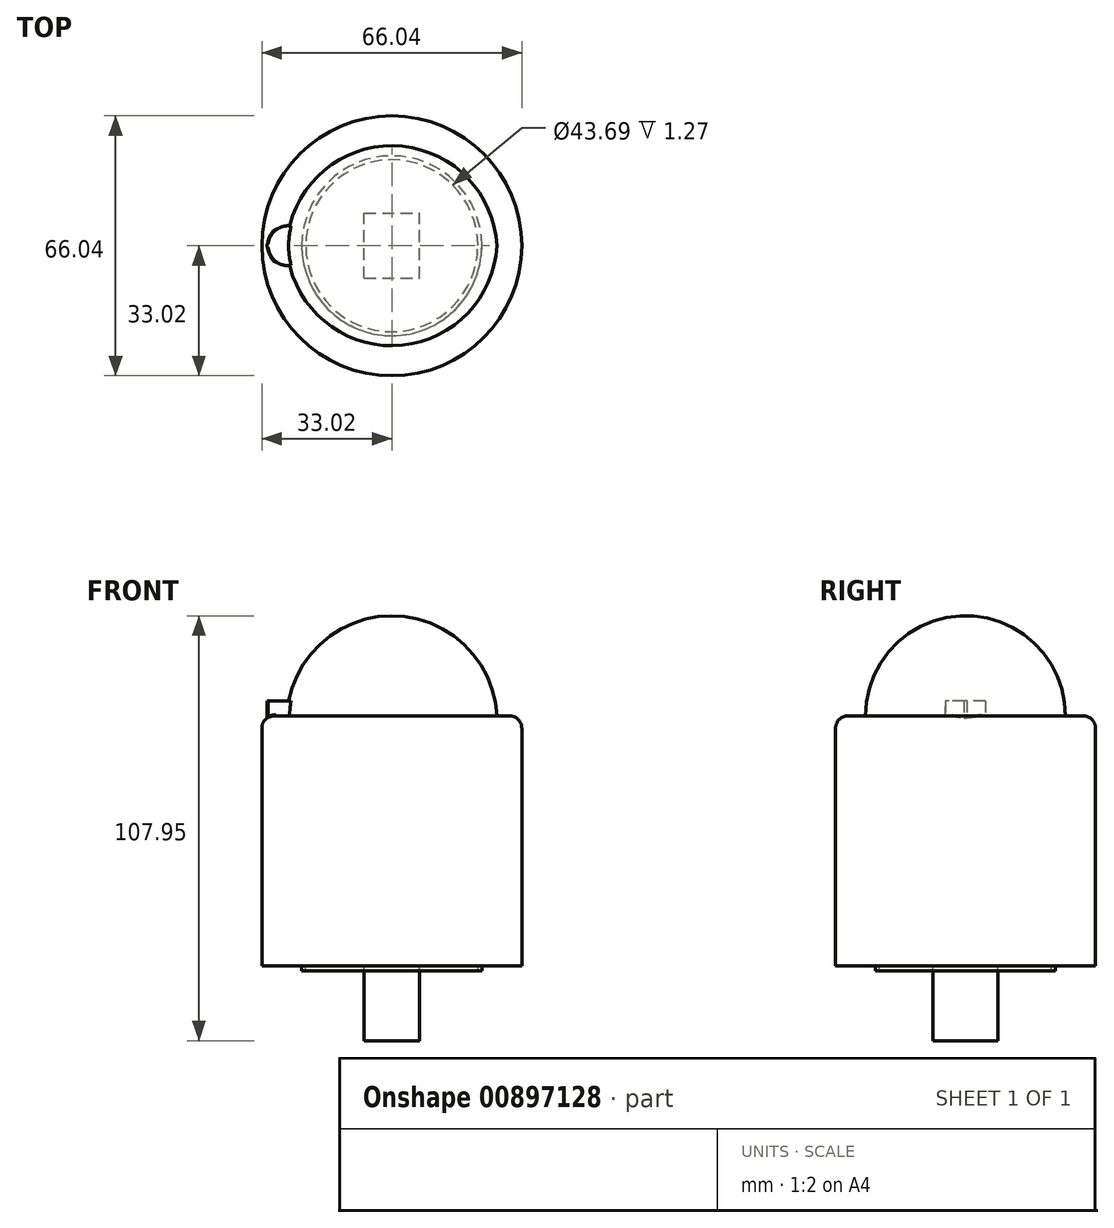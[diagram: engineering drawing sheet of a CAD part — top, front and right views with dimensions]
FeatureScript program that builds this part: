
annotation { "Feature Type Name" : "Feature", "Feature Type Description" : "" }
export const myFeature = defineFeature(function(context is Context, id is Id, definition is map)
    precondition{}
    {
        {
            var Q0;
            Q0=qCreatedBy(makeId("Top.planeOp"),FACE);
            var sketch = newSketch(context, id + "F0", { "sketchPlane" : qUnion([Q0])});
            skCircle(sketch, "E0", {"center": v(0, 0) * mm, "radius": 33.02 * mm});
            skSolve(sketch);
        }
        {
            var Q0;
            Q0=makeQuery(id+"F0.imprint","IMPRINT",FACE,{"disambiguationData":[TD([[makeQuery(id+"F0.imprint","IMPRINT",EDGE,{"derivedFrom":sQuery(id+"F0.wireOp",EDGE,"E0")}),1.0]])]});
            extrude(context, id + "F1", {"entities" : qUnion([Q0]), "depth" : 63.5 * mm, "offsetDistance" : 25.4 * mm});
        }
        {
            var Q0;
            Q0=makeQuery(id+"F1.opExtrude","CAP_FACE",FACE,{"disambiguationData":[OSD([sQuery(id+"F0.wireOp",EDGE,"E0")])],"isStart":false});
            var sketch = newSketch(context, id + "F2", { "sketchPlane" : qUnion([Q0])});
            skCircle(sketch, "E1", {"center": v(0, 0) * mm, "radius": 26.67 * mm});
            skSolve(sketch);
        }
        {
            var Q0;
            Q0=qCreatedBy(makeId("Front.planeOp"),FACE);
            var sketch = newSketch(context, id + "F3", { "sketchPlane" : qUnion([Q0])});
            skArc(sketch, "E2", {"start": v(26.67, 63.5) * mm, "mid": v(0, 88.9) * mm, "end": v(-26.67, 63.5) * mm});
            skLineSegment(sketch, "E3", {"start": v(-26.67, 63.5) * mm, "end": v(26.67, 63.5) * mm});
            skSolve(sketch);
        }
        {
            var Q0;
            Q0=makeQuery(id+"F3.imprint","IMPRINT",FACE,{"disambiguationData":[TD([[makeQuery(id+"F3.imprint","IMPRINT",EDGE,{"derivedFrom":sQuery(id+"F3.wireOp",EDGE,"E2")}),1.0]])]});
            var Q1;
            Q1=sQuery(id+"F3.wireOp",EDGE,"E3");
            revolve(context, id + "F4", {"operationType" : NewBodyOperationType.ADD, "surfaceOperationType" : NewSurfaceOperationType.NEW, "entities" : qUnion([Q0]), "axis" : qUnion([Q1]), "revolveType" : RevolveType.FULL});
        }
        {
            var Q0;
            Q0=makeQuery(id+"F2.imprint","IMPRINT",FACE,{"disambiguationData":[TD([[makeQuery(id+"F2.imprint","IMPRINT",EDGE,{"derivedFrom":sQuery(id+"F2.wireOp",EDGE,"E1")}),-1.0]])]});
            cPlane(context, id + "F5", {"entities" : qUnion([Q0]), "cplaneType" : CPlaneType.OFFSET, "offset" : 0 * mm, "width" : 152.4 * mm, "height" : 152.4 * mm});
        }
        {
            var Q0;
            Q0=makeQuery(id+"F1.opExtrude","CAP_EDGE",EDGE,{"disambiguationData":[OSD([sQuery(id+"F0.wireOp",EDGE,"E0")])],"isStart":false});
            fillet(context, id + "F6", {"entities" : qUnion([Q0]), "radius" : 3.17 * mm, "tangentPropagation" : true, "allowEdgeOverflow" : false});
        }
        {
            var Q0;
            Q0=qCreatedBy(id+"F5.planeOp",FACE);
            var sketch = newSketch(context, id + "F7", { "sketchPlane" : qUnion([Q0])});
            skCircle(sketch, "E4", {"center": v(-26.35, 0) * mm, "radius": 5.08 * mm});
            skPoint(sketch, "E5", {"position": v(-31.43, 0) * mm});
            skLineSegment(sketch, "E6", {"start": v(-29.85, 0) * mm, "end": v(-31.43, 0) * mm, "construction": true});
            skSolve(sketch);
        }
        {
            var Q0;
            Q0=makeQuery(id+"F1.opExtrude","CAP_FACE",FACE,{"disambiguationData":[OSD([sQuery(id+"F0.wireOp",EDGE,"E0")])],"isStart":true});
            var sketch = newSketch(context, id + "F8", { "sketchPlane" : qUnion([Q0])});
            skLineSegment(sketch, "E7.bottom", {"start": v(-6.99, 8.26) * mm, "end": v(6.99, 8.26) * mm});
            skLineSegment(sketch, "E7.top", {"start": v(-6.99, -8.26) * mm, "end": v(6.99, -8.26) * mm});
            skLineSegment(sketch, "E7.left", {"start": v(-6.99, 8.26) * mm, "end": v(-6.99, -8.26) * mm});
            skLineSegment(sketch, "E7.right", {"start": v(6.99, 8.26) * mm, "end": v(6.99, -8.26) * mm});
            skPoint(sketch, "E7.middle", {"position": v(0, 0) * mm});
            skSolve(sketch);
        }
        {
            var Q0;
            Q0=makeQuery(id+"F8.imprint","IMPRINT",FACE,{"disambiguationData":[TD([[makeQuery(id+"F8.imprint","IMPRINT",EDGE,{"derivedFrom":sQuery(id+"F8.wireOp",EDGE,"E7.bottom")}),-1.0]])]});
            extrude(context, id + "F9", {"entities" : qUnion([Q0]), "operationType" : NewBodyOperationType.ADD, "depth" : 19.05 * mm, "offsetDistance" : 25.4 * mm});
        }
        {
            var Q0;
            Q0=makeQuery(id+"F1.opExtrude","CAP_FACE",FACE,{"disambiguationData":[OSD([sQuery(id+"F0.wireOp",EDGE,"E0")])],"isStart":true});
            var sketch = newSketch(context, id + "F10", { "sketchPlane" : qUnion([Q0])});
            skCircle(sketch, "E8", {"center": v(0, 0) * mm, "radius": 22.86 * mm});
            skCircle(sketch, "E9", {"center": v(0, 0) * mm, "radius": 21.84 * mm});
            skSolve(sketch);
        }
        {
            var Q0;
            Q0=makeQuery(id+"F10.imprint","IMPRINT",FACE,{"disambiguationData":[TD([[makeQuery(id+"F10.imprint","IMPRINT",EDGE,{"derivedFrom":sQuery(id+"F10.wireOp",EDGE,"E8")}),1.0]])]});
            extrude(context, id + "F11", {"entities" : qUnion([Q0]), "operationType" : NewBodyOperationType.ADD, "depth" : 1.27 * mm, "offsetDistance" : 25.4 * mm});
        }
        {
            var Q0;
            Q0 = qSketchRegion(id + "F7", true);
            extrude(context, id + "F12", {"entities" : qUnion([Q0]), "operationType" : NewBodyOperationType.ADD, "endBound" : BoundingType.SYMMETRIC, "depth" : 7.62 * mm, "offsetDistance" : 25.4 * mm});
        }
        {
            var Q0;
            Q0=makeQuery(id+"F12.boolean.opBoolean","INTERSECT",EDGE,{"derivedFrom":[makeQuery(id+"F6.opFillet","BLEND_FACE",FACE,{"disambiguationData":[OSD([sQuery(id+"F0.wireOp",EDGE,"E0")])]}),makeQuery(id+"F12.opExtrude","SWEPT_FACE",FACE,{"disambiguationData":[OSD([sQuery(id+"F7.wireOp",EDGE,"E4")])]})]});
            fillet(context, id + "F13", {"entities" : qUnion([Q0]), "radius" : 0.25 * mm, "tangentPropagation" : true, "allowEdgeOverflow" : false});
        }
        {
            var Q0;
            Q0=qCreatedBy(makeId("Right.planeOp"),FACE);
            cPlane(context, id + "F14", {"entities" : qUnion([Q0]), "cplaneType" : CPlaneType.OFFSET, "offset" : 31.75 * mm, "oppositeDirection" : true, "width" : 152.4 * mm, "height" : 152.4 * mm});
        }
        {
            var Q0;
            Q0=qCreatedBy(id+"F14.planeOp",FACE);
            var sketch = newSketch(context, id + "F15", { "sketchPlane" : qUnion([Q0])});
            skLineSegment(sketch, "E10.bottom", {"start": v(0.38, 67.3) * mm, "end": v(-0.38, 67.3) * mm});
            skLineSegment(sketch, "E10.top", {"start": v(0.38, 63) * mm, "end": v(-0.38, 63) * mm});
            skLineSegment(sketch, "E10.left", {"start": v(0.38, 67.3) * mm, "end": v(0.38, 63) * mm});
            skLineSegment(sketch, "E10.right", {"start": v(-0.38, 67.3) * mm, "end": v(-0.38, 63) * mm});
            skSolve(sketch);
        }
        {
            var Q0;
            Q0=makeQuery(id+"F15.imprint","IMPRINT",FACE,{"disambiguationData":[TD([[makeQuery(id+"F15.imprint","IMPRINT",EDGE,{"derivedFrom":sQuery(id+"F15.wireOp",EDGE,"E10.bottom")}),1.0]])]});
            extrude(context, id + "F16", {"entities" : qUnion([Q0]), "operationType" : NewBodyOperationType.ADD, "depth" : 25.4 * mm, "offsetDistance" : 25.4 * mm});
        }
    });
